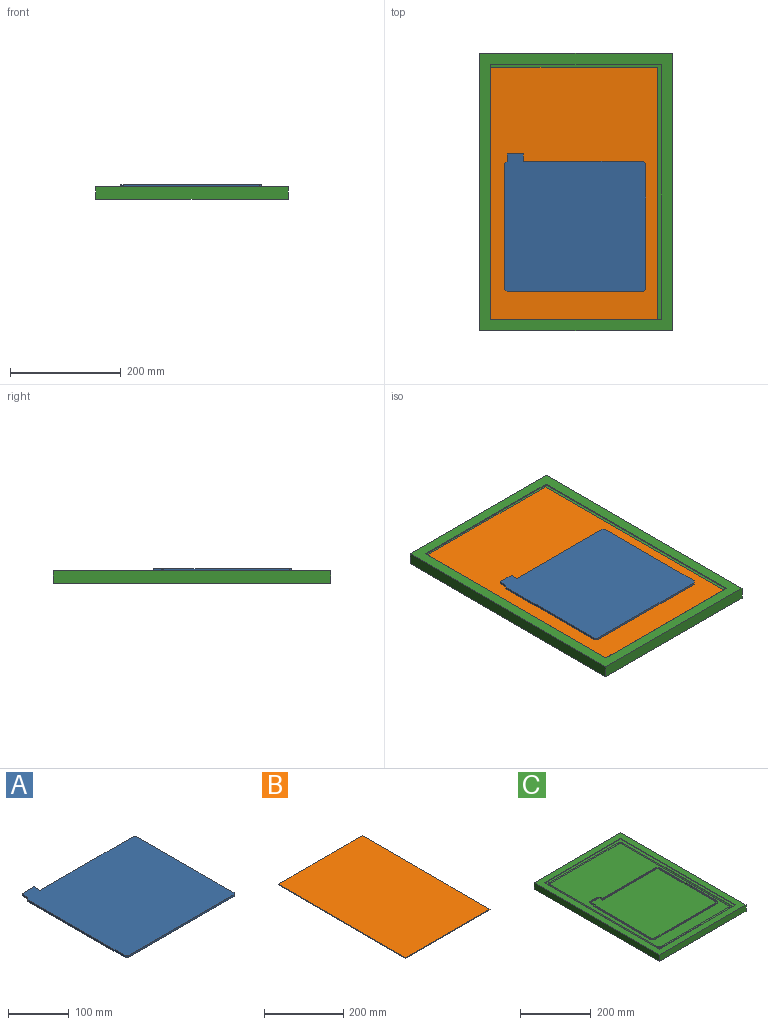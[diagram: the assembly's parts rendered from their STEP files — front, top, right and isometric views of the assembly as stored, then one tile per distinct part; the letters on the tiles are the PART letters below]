
ASSEMBLY  parts=3 mates=4
PART A: 16 faces, bbox 254x249.3x3.7 mm
  f0: plane 215.81x3.7mm, normal (0,1,0), area 798.5mm2, adj f2,f5,f10,f15
  f1: plane 12.89x3.7mm, normal (1,0,0), area 47.7mm2, adj f2,f5,f13,f15
  f2: plane 254x249.3mm, normal (0,0,1), area 60068.4mm2, adj f0,f1,f3,f4,f6,f7,f8,f9
  f3: plane 13.59x3.7mm, normal (-1,0,0), area 50.3mm2, adj f2,f5,f11,f14
  f4: plane 27.59x3.7mm, normal (0,1,0), area 102.1mm2, adj f2,f5,f13,f14
  f5: plane 254x249.3mm, normal (0,0,-1), area 60068.4mm2, adj f0,f1,f3,f4,f6,f7,f8,f9
  f6: plane 226.51x3.7mm, normal (-1,0,0), area 838.1mm2, adj f2,f5,f9,f11
  f7: plane 245.51x3.7mm, normal (0,-1,0), area 908.4mm2, adj f2,f5,f9,f12
  f8: plane 226.51x3.7mm, normal (1,0,0), area 838.1mm2, adj f2,f5,f10,f12
  f9: plane 4.24x4.24mm, normal (-0.71,-0.71,0), area 22.2mm2, adj f2,f5,f6,f7
  f10: plane 4.24x4.24mm, normal (0.71,0.71,0), area 22.2mm2, adj f0,f2,f5,f8
  f11: plane 4.24x4.24mm, normal (-0.71,0.71,0), area 22.2mm2, adj f2,f3,f5,f6
  f12: plane 4.24x4.24mm, normal (0.71,-0.71,0), area 22.2mm2, adj f2,f5,f7,f8
  f13: plane 3.7x0.71mm, normal (0.71,0.71,0), area 3.7mm2, adj f1,f2,f4,f5
  f14: plane 3.7x0.71mm, normal (-0.71,0.71,0), area 3.7mm2, adj f2,f3,f4,f5
  f15: plane 3.7x0.71mm, normal (0.71,0.71,0), area 3.7mm2, adj f0,f1,f2,f5
PART B: 6 faces, bbox 300x455x2 mm
  f0: plane 455x2mm, normal (-1,0,0), area 910mm2, adj f1,f3,f4,f5
  f1: plane 300x2mm, normal (0,-1,0), area 600mm2, adj f0,f2,f4,f5
  f2: plane 455x2mm, normal (1,0,0), area 910mm2, adj f1,f3,f4,f5
  f3: plane 300x2mm, normal (0,1,0), area 600mm2, adj f0,f2,f4,f5
  f4: plane 455x300mm, normal (0,0,1), area 136500mm2, adj f0,f1,f2,f3
  f5: plane 455x300mm, normal (0,0,-1), area 136500mm2, adj f0,f1,f2,f3
PART C: 48 faces, bbox 347x500x22 mm
  f0: plane 460x307mm, normal (0,0,1), area 9299.8mm2, adj f1,f2,f3,f8,f11,f12,f13,f14
  f1: plane 460x2mm, normal (-1,0,0), area 920mm2, adj f0,f2,f8,f9
  f2: plane 307x2mm, normal (0,1,0), area 614mm2, adj f0,f1,f3,f9
  f3: plane 460x2mm, normal (1,0,0), area 920mm2, adj f0,f2,f8,f9
  f4: plane 347x22mm, normal (0,1,0), area 7634mm2, adj f5,f7,f9,f10
  f5: plane 500x22mm, normal (-1,0,0), area 11000mm2, adj f4,f6,f9,f10
  f6: plane 347x22mm, normal (0,-1,0), area 7634mm2, adj f5,f7,f9,f10
  f7: plane 500x22mm, normal (1,0,0), area 11000mm2, adj f4,f6,f9,f10
  f8: plane 307x2mm, normal (0,-1,0), area 614mm2, adj f0,f1,f3,f9
  f9: plane 500x347mm, normal (0,0,1), area 32280mm2, adj f1,f2,f3,f4,f5,f6,f7,f8
  f10: plane 500x347mm, normal (0,0,-1), area 173500mm2, adj f4,f5,f6,f7
  f11: torus R=7.5mm, axis (0,0,-1), area 92.5mm2, adj f0,f12,f18,f19
  f12: cylinder r=2.5mm len=274mm, axis (-1,0,0), area 2152mm2, adj f0,f11,f13,f19
  f13: torus R=7.5mm, axis (0,0,-1), area 92.5mm2, adj f0,f12,f14,f19
  f14: cylinder r=2.5mm len=429mm, axis (0,-1,0), area 3369.4mm2, adj f0,f13,f15,f19
  f15: torus R=7.5mm, axis (0,0,-1), area 92.5mm2, adj f0,f14,f16,f19
  f16: cylinder r=2.5mm len=274mm, axis (1,0,0), area 2152mm2, adj f0,f15,f17,f19
  f17: torus R=7.5mm, axis (0,0,-1), area 92.5mm2, adj f0,f16,f18,f19
  f18: cylinder r=2.5mm len=429mm, axis (0,1,0), area 3369.4mm2, adj f0,f11,f17,f19
  f19: plane 439x284mm, normal (0,0,1), area 58498.2mm2, adj f11,f12,f13,f14,f15,f16,f17,f18
  f20: plane 7.76x7.76mm, normal (-0.71,0.71,0), area 36.2mm2, adj f19,f21,f45,f46
  f21: plane 231.49x3.3mm, normal (-1,0,0), area 763.9mm2, adj f19,f20,f22,f46
  f22: plane 7.76x7.76mm, normal (-0.71,-0.71,0), area 36.2mm2, adj f19,f21,f23,f46
  f23: plane 213x3.3mm, normal (0,-1,0), area 702.9mm2, adj f19,f22,f24,f46
  f24: plane 10.08x3.3mm, normal (-1,0,0), area 33.3mm2, adj f19,f23,f25,f46
  f25: plane 4.22x4.22mm, normal (-0.71,-0.71,0), area 19.7mm2, adj f19,f24,f26,f46
  f26: plane 32.56x3.3mm, normal (0,-1,0), area 107.4mm2, adj f19,f25,f27,f46
  f27: plane 4.22x4.22mm, normal (0.71,-0.71,0), area 19.7mm2, adj f19,f26,f28,f46
  f28: plane 13.59x3.3mm, normal (1,0,0), area 44.9mm2, adj f19,f27,f29,f46
  f29: plane 4.24x4.24mm, normal (0.71,-0.71,0), area 19.8mm2, adj f19,f28,f30,f46
  f30: plane 231.49x3.3mm, normal (1,0,0), area 763.9mm2, adj f19,f29,f31,f46
  f31: plane 7.76x7.76mm, normal (0.71,0.71,0), area 36.2mm2, adj f19,f30,f45,f46
  f32: plane 13.59x3.3mm, normal (1,0,0), area 44.9mm2, adj f33,f44,f46,f47
  f33: plane 216.51x3.3mm, normal (0,1,0), area 714.5mm2, adj f32,f34,f46,f47
  f34: plane 4.24x4.24mm, normal (0.71,0.71,0), area 19.8mm2, adj f33,f35,f46,f47
  f35: plane 226.51x3.3mm, normal (1,0,0), area 747.5mm2, adj f34,f36,f46,f47
  f36: plane 4.24x4.24mm, normal (0.71,-0.71,0), area 19.8mm2, adj f35,f37,f46,f47
  f37: plane 245.51x3.3mm, normal (0,-1,0), area 810.2mm2, adj f36,f38,f46,f47
  f38: plane 4.24x4.24mm, normal (-0.71,-0.71,0), area 19.8mm2, adj f37,f39,f46,f47
  f39: plane 226.51x3.3mm, normal (-1,0,0), area 747.5mm2, adj f38,f40,f46,f47
  f40: plane 4.24x4.24mm, normal (-0.71,0.71,0), area 19.8mm2, adj f39,f41,f46,f47
  f41: plane 13.59x3.3mm, normal (-1,0,0), area 44.9mm2, adj f40,f42,f46,f47
  f42: plane 3.3x0.71mm, normal (-0.71,0.71,0), area 3.3mm2, adj f41,f43,f46,f47
  f43: plane 27.59x3.3mm, normal (0,1,0), area 91mm2, adj f42,f44,f46,f47
  f44: plane 3.3x0.71mm, normal (0.71,0.71,0), area 3.3mm2, adj f32,f43,f46,f47
  f45: plane 250.49x3.3mm, normal (0,1,0), area 826.6mm2, adj f19,f20,f31,f46
  f46: plane 266x261.3mm, normal (0,0,1), area 6088.1mm2, adj f20,f21,f22,f23,f24,f25,f26,f27
  f47: plane 254x249.3mm, normal (0,0,1), area 60068.2mm2, adj f32,f33,f34,f35,f36,f37,f38,f39
PLACE A t=(45,70,22)mm
PLACE B t=(20,20,20)mm
PLACE C t=(21,21,18)mm
MATE planar A.f5 <-> B.f4  axis (0,0,-1) through (171.25,188.36,22)mm
MATE planar A.f6 <-> C.f39  axis (-1,0,0) through (45,187.5,23.85)mm
MATE fastened B.f5 <-> C.f0  axis (0,0,-1) through (20,20,20)mm
MATE planar A.f7 <-> C.f37  axis (0,-1,0) through (172,70,23.85)mm
